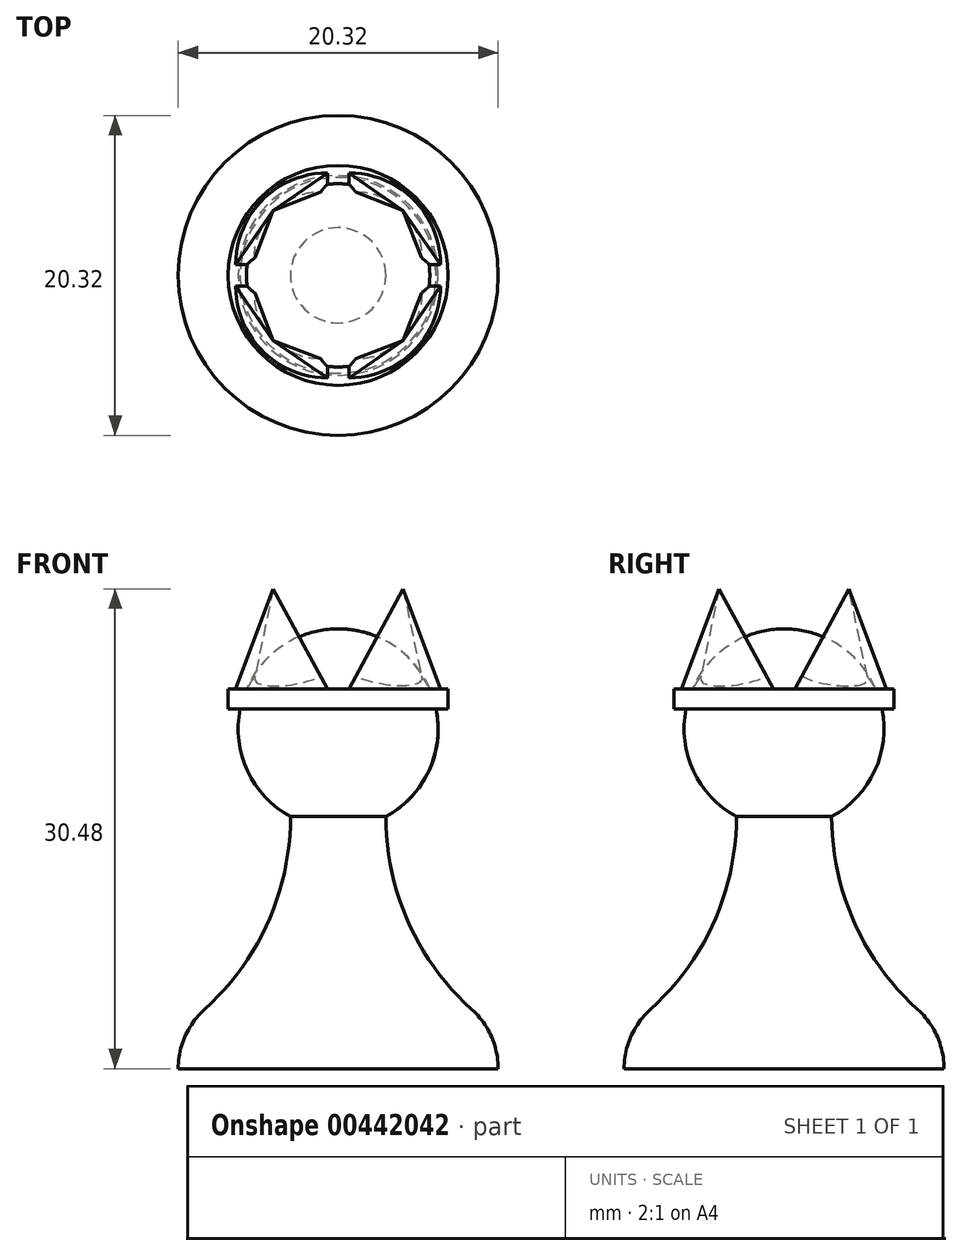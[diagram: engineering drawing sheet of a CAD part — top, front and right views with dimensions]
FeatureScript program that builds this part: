
annotation { "Feature Type Name" : "Feature", "Feature Type Description" : "" }
export const myFeature = defineFeature(function(context is Context, id is Id, definition is map)
    precondition{}
    {
        {
            var Q0;
            Q0=qCreatedBy(makeId("Front.planeOp"),FACE);
            var sketch = newSketch(context, id + "F0", { "sketchPlane" : qUnion([Q0])});
            skArc(sketch, "E0", {"start": v(0, 27.94) * mm, "mid": v(-6.35, 21.6) * mm, "end": v(0, 15.24) * mm});
            skLineSegment(sketch, "E1", {"start": v(0, 0) * mm, "end": v(-10.16, 0) * mm});
            skArc(sketch, "E2", {"start": v(-8.48, 3.77) * mm, "mid": v(-9.72, 2.07) * mm, "end": v(-10.16, 0) * mm});
            skArc(sketch, "E3", {"start": v(-8.48, 3.77) * mm, "mid": v(-4.45, 9.31) * mm, "end": v(-3.02, 16) * mm});
            skLineSegment(sketch, "E4", {"start": v(-3.02, 16) * mm, "end": v(-3.02, 0) * mm, "construction": true});
            skLineSegment(sketch, "E5", {"start": v(0, 27.94) * mm, "end": v(0, 0) * mm});
            skLineSegment(sketch, "E6", {"start": v(-10.16, 0) * mm, "end": v(-10.16, 3.2) * mm, "construction": true});
            skPoint(sketch, "E7", {"position": v(-6.35, 21.6) * mm});
            skSolve(sketch);
        }
        {
            var Q0;
            Q0=qSketchRegion(id+"F0",true);
            var Q1;
            Q1=sQuery(id+"F0.wireOp",EDGE,"E5");
            revolve(context, id + "F1", {"entities" : qUnion([Q0]), "axis" : qUnion([Q1]), "revolveType" : RevolveType.FULL});
        }
        {
            var Q0;
            Q0=qCreatedBy(makeId("Top.planeOp"),FACE);
            cPlane(context, id + "F2", {"entities" : qUnion([Q0]), "cplaneType" : CPlaneType.OFFSET, "offset" : 22.86 * mm, "width" : 152.4 * mm, "height" : 152.4 * mm});
        }
        {
            var Q0;
            Q0=qCreatedBy(id+"F2.planeOp",FACE);
            var sketch = newSketch(context, id + "F3", { "sketchPlane" : qUnion([Q0])});
            skCircle(sketch, "E8", {"center": v(0, 0) * mm, "radius": 6.99 * mm});
            skCircle(sketch, "E9", {"center": v(0, 0) * mm, "radius": 5.72 * mm});
            skLineSegment(sketch, "E10", {"start": v(0, 6.99) * mm, "end": v(0, 5.72) * mm});
            skLineSegment(sketch, "E11", {"start": v(5.72, 0) * mm, "end": v(6.99, 0) * mm});
            skLineSegment(sketch, "E12", {"start": v(0, -5.72) * mm, "end": v(0, -6.99) * mm});
            skLineSegment(sketch, "E13", {"start": v(-6.99, 0) * mm, "end": v(-5.72, 0) * mm});
            skSolve(sketch);
        }
        {
            var Q0;
            Q0=qCreatedBy(makeId("Top.planeOp"),FACE);
            cPlane(context, id + "F4", {"entities" : qUnion([Q0]), "cplaneType" : CPlaneType.OFFSET, "offset" : 30.48 * mm, "width" : 152.4 * mm, "height" : 152.4 * mm});
        }
        {
            var Q0;
            Q0=qCreatedBy(id+"F4.planeOp",FACE);
            var sketch = newSketch(context, id + "F5", { "sketchPlane" : qUnion([Q0])});
            skCircle(sketch, "E14.cCircle", {"center": v(0, 0) * mm, "radius": 4.13 * mm, "construction": true});
            skLineSegment(sketch, "E14.0", {"start": v(4.13, 4.13) * mm, "end": v(4.13, -4.13) * mm});
            skLineSegment(sketch, "E14.1", {"start": v(4.13, -4.13) * mm, "end": v(-4.13, -4.13) * mm});
            skLineSegment(sketch, "E14.2", {"start": v(-4.13, -4.13) * mm, "end": v(-4.13, 4.13) * mm});
            skLineSegment(sketch, "E14.3", {"start": v(-4.13, 4.13) * mm, "end": v(4.13, 4.13) * mm});
            skPoint(sketch, "E14.0.midPoint", {"position": v(4.13, 0) * mm});
            skSolve(sketch);
        }
        {
            var Q0;
            Q0 = qSketchRegion(id + "F3", true);
            extrude(context, id + "F6", {"entities" : qUnion([Q0]), "operationType" : NewBodyOperationType.ADD, "depth" : 1.27 * mm});
        }
        {
            var Q0;
            Q0=sQuery(id+"F5.wireOp",VERTEX,"E14.2.start");
            var Q1;
            {var subQ0=sQuery(id+"F3.wireOp",EDGE,"E12");Q1=makeQuery(id+"F3.imprint","IMPRINT",FACE,{"disambiguationData":[TD([[makeQuery(id+"F3.imprint","IMPRINT",EDGE,{"derivedFrom":subQ0}),-1.0]])]});}
            loft(context, id + "F7", {"operationType" : NewBodyOperationType.ADD, "sheetProfilesArray" : [{ "sheetProfileEntities" : qUnion([Q0]) }, { "sheetProfileEntities" : qUnion([Q1]) }]});
        }
        {
            var Q0;
            Q0=sQuery(id+"F5.wireOp",VERTEX,"E14.1.start");
            var Q1;
            {var subQ0=sQuery(id+"F3.wireOp",EDGE,"E11");Q1=makeQuery(id+"F3.imprint","IMPRINT",FACE,{"disambiguationData":[TD([[makeQuery(id+"F3.imprint","IMPRINT",EDGE,{"derivedFrom":subQ0}),-1.0]])]});}
            loft(context, id + "F8", {"operationType" : NewBodyOperationType.ADD, "sheetProfilesArray" : [{ "sheetProfileEntities" : qUnion([Q0]) }, { "sheetProfileEntities" : qUnion([Q1]) }]});
        }
        {
            var Q0;
            {var subQ0=sQuery(id+"F3.wireOp",EDGE,"E10");Q0=makeQuery(id+"F3.imprint","IMPRINT",FACE,{"disambiguationData":[TD([[makeQuery(id+"F3.imprint","IMPRINT",EDGE,{"derivedFrom":subQ0}),-1.0]])]});}
            var Q1;
            Q1=sQuery(id+"F5.wireOp",VERTEX,"E14.3.start");
            loft(context, id + "F9", {"operationType" : NewBodyOperationType.ADD, "sheetProfilesArray" : [{ "sheetProfileEntities" : qUnion([Q0]) }, { "sheetProfileEntities" : qUnion([Q1]) }]});
        }
        {
            var Q0;
            {var subQ0=sQuery(id+"F3.wireOp",EDGE,"E10");Q0=makeQuery(id+"F3.imprint","IMPRINT",FACE,{"disambiguationData":[TD([[makeQuery(id+"F3.imprint","IMPRINT",EDGE,{"derivedFrom":subQ0}),1.0]])]});}
            var Q1;
            Q1=sQuery(id+"F5.wireOp",VERTEX,"E14.0.start");
            loft(context, id + "F10", {"operationType" : NewBodyOperationType.ADD, "sheetProfilesArray" : [{ "sheetProfileEntities" : qUnion([Q0]) }, { "sheetProfileEntities" : qUnion([Q1]) }]});
        }
    });
